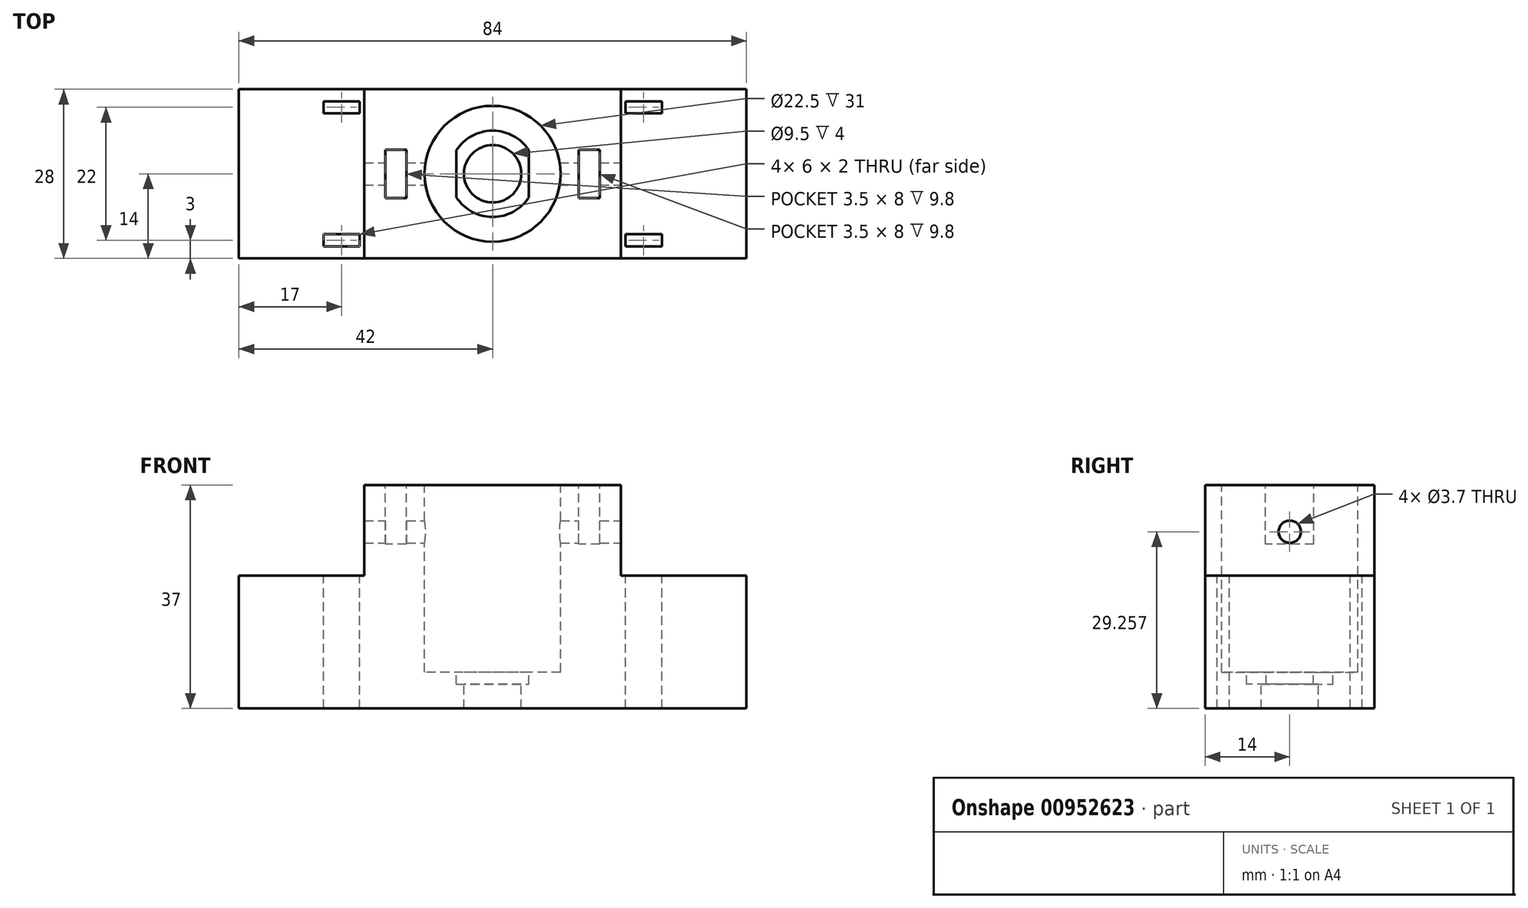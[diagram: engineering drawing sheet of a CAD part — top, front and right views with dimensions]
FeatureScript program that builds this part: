
annotation { "Feature Type Name" : "Feature", "Feature Type Description" : "" }
export const myFeature = defineFeature(function(context is Context, id is Id, definition is map)
    precondition{}
    {
        {
            var Q0;
            Q0=qCreatedBy(makeId("Top.planeOp"),FACE);
            var sketch = newSketch(context, id + "F0", { "sketchPlane" : qUnion([Q0])});
            skCircle(sketch, "E0", {"center": v(0, 0) * mm, "radius": 14 * mm});
            skLineSegment(sketch, "E1.bottom", {"start": v(42, -14) * mm, "end": v(-42, -14) * mm});
            skLineSegment(sketch, "E1.top", {"start": v(42, 14) * mm, "end": v(-42, 14) * mm});
            skLineSegment(sketch, "E1.left", {"start": v(42, -14) * mm, "end": v(42, 14) * mm});
            skLineSegment(sketch, "E1.right", {"start": v(-42, -14) * mm, "end": v(-42, 14) * mm});
            skSolve(sketch);
        }
        {
            var Q0;
            Q0 = qSketchRegion(id + "F0", true);
            var Q1;
            Q1 = qSketchRegion(id + "F3", true);
            var Q2;
            Q2 = qSketchRegion(id + "F2", true);
            extrude(context, id + "F1", {"entities" : qUnion([Q0, Q1, Q2]), "depth" : 22 * mm, "offsetDistance" : 25.4 * mm});
        }
        {
            var Q0;
            Q0=makeQuery(id+"F1.opExtrude","CAP_FACE",FACE,{"disambiguationData":[OSD([sQuery(id+"F0.wireOp",EDGE,"E1.bottom"),sQuery(id+"F0.wireOp",EDGE,"E1.top"),sQuery(id+"F0.wireOp",EDGE,"E1.left"),sQuery(id+"F0.wireOp",EDGE,"E1.right")])],"isStart":false});
            var sketch = newSketch(context, id + "F2", { "sketchPlane" : qUnion([Q0])});
            skArc(sketch, "E2", {"start": v(-6, -3.89) * mm, "mid": v(0, -7.15) * mm, "end": v(6, -3.89) * mm});
            skLineSegment(sketch, "E3.left", {"start": v(6, 3.89) * mm, "end": v(6, -3.89) * mm});
            skLineSegment(sketch, "E3.right", {"start": v(-6, 3.89) * mm, "end": v(-6, -3.89) * mm});
            skArc(sketch, "E4.trimOffspring", {"start": v(6, 3.89) * mm, "mid": v(0, 7.15) * mm, "end": v(-6, 3.89) * mm});
            skSolve(sketch);
        }
        {
            var Q0;
            Q0=makeQuery(id+"F1.opExtrude","CAP_FACE",FACE,{"disambiguationData":[OSD([sQuery(id+"F0.wireOp",EDGE,"E1.bottom"),sQuery(id+"F0.wireOp",EDGE,"E1.top"),sQuery(id+"F0.wireOp",EDGE,"E1.left"),sQuery(id+"F0.wireOp",EDGE,"E1.right")])],"isStart":false});
            var sketch = newSketch(context, id + "F3", { "sketchPlane" : qUnion([Q0])});
            skCircle(sketch, "E5", {"center": v(0, 0) * mm, "radius": 11.25 * mm});
            skSolve(sketch);
        }
        {
            var Q0;
            Q0 = qSketchRegion(id + "F3", true);
            extrude(context, id + "F4", {"entities" : qUnion([Q0]), "operationType" : NewBodyOperationType.REMOVE, "oppositeDirection" : true, "depth" : 16 * mm, "offsetDistance" : 25.4 * mm});
        }
        {
            var Q0;
            Q0 = qSketchRegion(id + "F2", true);
            extrude(context, id + "F5", {"entities" : qUnion([Q0]), "operationType" : NewBodyOperationType.REMOVE, "oppositeDirection" : true, "depth" : 18 * mm, "offsetDistance" : 25.4 * mm});
        }
        {
            var Q0;
            Q0=makeQuery(id+"F5.boolean.opBoolean","COPY",FACE,{"derivedFrom":makeQuery(id+"F5.opExtrude","CAP_FACE",FACE,{"disambiguationData":[OSD([sQuery(id+"F2.wireOp",EDGE,"E2"),sQuery(id+"F2.wireOp",EDGE,"E3.left"),sQuery(id+"F2.wireOp",EDGE,"E3.right"),sQuery(id+"F2.wireOp",EDGE,"E4.trimOffspring")])],"isStart":false})});
            var sketch = newSketch(context, id + "F6", { "sketchPlane" : qUnion([Q0])});
            skCircle(sketch, "E6", {"center": v(0, 0) * mm, "radius": 4.75 * mm});
            skSolve(sketch);
        }
        {
            var Q0;
            Q0 = qSketchRegion(id + "F6", true);
            extrude(context, id + "F7", {"entities" : qUnion([Q0]), "operationType" : NewBodyOperationType.REMOVE, "oppositeDirection" : true, "depth" : 4 * mm, "offsetDistance" : 25.4 * mm});
        }
        {
            var Q0;
            Q0=makeQuery(id+"F1.opExtrude","CAP_FACE",FACE,{"disambiguationData":[OSD([sQuery(id+"F0.wireOp",EDGE,"E1.bottom"),sQuery(id+"F0.wireOp",EDGE,"E1.top"),sQuery(id+"F0.wireOp",EDGE,"E1.left"),sQuery(id+"F0.wireOp",EDGE,"E1.right")])],"isStart":false});
            var sketch = newSketch(context, id + "F8", { "sketchPlane" : qUnion([Q0])});
            skPoint(sketch, "E7", {"position": v(-25, 0) * mm});
            skPoint(sketch, "E8", {"position": v(25, 0) * mm});
            skLineSegment(sketch, "E9", {"start": v(0, 0) * mm, "end": v(-25, 0) * mm});
            skLineSegment(sketch, "E10", {"start": v(-25, 0) * mm, "end": v(-25, 19.23) * mm});
            skLineSegment(sketch, "E11", {"start": v(-25, 0) * mm, "end": v(-25, -16.03) * mm});
            skLineSegment(sketch, "E12", {"start": v(25, 0) * mm, "end": v(25, 19.12) * mm});
            skLineSegment(sketch, "E13", {"start": v(25, 0) * mm, "end": v(25, -19.57) * mm});
            skPoint(sketch, "E14.orphan", {"position": v(-23.51, -11) * mm});
            skPoint(sketch, "E15", {"position": v(25, -11) * mm});
            skPoint(sketch, "E16", {"position": v(25, 11) * mm});
            skPoint(sketch, "E17", {"position": v(-25, 11) * mm});
            skPoint(sketch, "E18.orphan", {"position": v(23.65, -11) * mm});
            skLineSegment(sketch, "E19.bottom", {"start": v(28, -12) * mm, "end": v(22, -12) * mm});
            skLineSegment(sketch, "E19.top", {"start": v(28, -10) * mm, "end": v(22, -10) * mm});
            skLineSegment(sketch, "E19.left", {"start": v(28, -12) * mm, "end": v(28, -10) * mm});
            skLineSegment(sketch, "E19.right", {"start": v(22, -12) * mm, "end": v(22, -10) * mm});
            skPoint(sketch, "E20.start.orphan", {"position": v(23.65, 11) * mm});
            skLineSegment(sketch, "E21.bottom", {"start": v(28, 10) * mm, "end": v(22, 10) * mm});
            skLineSegment(sketch, "E21.top", {"start": v(28, 12) * mm, "end": v(22, 12) * mm});
            skLineSegment(sketch, "E21.left", {"start": v(28, 10) * mm, "end": v(28, 12) * mm});
            skLineSegment(sketch, "E21.right", {"start": v(22, 10) * mm, "end": v(22, 12) * mm});
            skPoint(sketch, "E22.start.orphan", {"position": v(-23.51, 11) * mm});
            skLineSegment(sketch, "E23.bottom", {"start": v(-22, 10) * mm, "end": v(-28, 10) * mm});
            skLineSegment(sketch, "E23.top", {"start": v(-22, 12) * mm, "end": v(-28, 12) * mm});
            skLineSegment(sketch, "E23.left", {"start": v(-22, 10) * mm, "end": v(-22, 12) * mm});
            skLineSegment(sketch, "E23.right", {"start": v(-28, 10) * mm, "end": v(-28, 12) * mm});
            skLineSegment(sketch, "E24.bottom", {"start": v(-22, -12) * mm, "end": v(-28, -12) * mm});
            skLineSegment(sketch, "E24.top", {"start": v(-22, -10) * mm, "end": v(-28, -10) * mm});
            skLineSegment(sketch, "E24.left", {"start": v(-22, -12) * mm, "end": v(-22, -10) * mm});
            skLineSegment(sketch, "E24.right", {"start": v(-28, -12) * mm, "end": v(-28, -10) * mm});
            skPoint(sketch, "E24.middle", {"position": v(-25, -11) * mm});
            skSolve(sketch);
        }
        {
            var Q0;
            Q0 = qSketchRegion(id + "F8", true);
            extrude(context, id + "F9", {"entities" : qUnion([Q0]), "operationType" : NewBodyOperationType.REMOVE, "oppositeDirection" : true, "depth" : 22 * mm, "offsetDistance" : 25.4 * mm});
        }
        {
            var Q0;
            Q0=makeQuery(id+"F1.opExtrude","CAP_FACE",FACE,{"disambiguationData":[OSD([sQuery(id+"F0.wireOp",EDGE,"E1.bottom"),sQuery(id+"F0.wireOp",EDGE,"E1.top"),sQuery(id+"F0.wireOp",EDGE,"E1.left"),sQuery(id+"F0.wireOp",EDGE,"E1.right")])],"isStart":false});
            var sketch = newSketch(context, id + "F10", { "sketchPlane" : qUnion([Q0])});
            skLineSegment(sketch, "E25.bottom", {"start": v(21.25, -14) * mm, "end": v(-21.25, -14) * mm});
            skLineSegment(sketch, "E25.top", {"start": v(21.25, 14) * mm, "end": v(-21.25, 14) * mm});
            skLineSegment(sketch, "E25.left", {"start": v(21.25, -14) * mm, "end": v(21.25, 14) * mm});
            skLineSegment(sketch, "E25.right", {"start": v(-21.25, -14) * mm, "end": v(-21.25, 14) * mm});
            skPoint(sketch, "E25.middle", {"position": v(0, 0) * mm});
            skLineSegment(sketch, "E26", {"start": v(11.25, 0) * mm, "end": v(21.25, 0) * mm});
            skSolve(sketch);
        }
        {
            var Q0;
            Q0 = qSketchRegion(id + "F10", true);
            extrude(context, id + "F11", {"entities" : qUnion([Q0]), "operationType" : NewBodyOperationType.ADD, "depth" : 15 * mm, "offsetDistance" : 25.4 * mm});
        }
        {
            var Q0;
            Q0=makeQuery(id+"F11.opExtrude","CAP_FACE",FACE,{"disambiguationData":[OSD([sQuery(id+"F10.wireOp",EDGE,"E25.bottom"),sQuery(id+"F10.wireOp",EDGE,"E25.top"),sQuery(id+"F10.wireOp",EDGE,"E25.left"),sQuery(id+"F10.wireOp",EDGE,"E25.right")])],"isStart":false});
            var sketch = newSketch(context, id + "F12", { "sketchPlane" : qUnion([Q0])});
            skCircle(sketch, "E27", {"center": v(0, 0) * mm, "radius": 11.25 * mm});
            skSolve(sketch);
        }
        {
            var Q0;
            Q0 = qSketchRegion(id + "F12", true);
            extrude(context, id + "F13", {"entities" : qUnion([Q0]), "operationType" : NewBodyOperationType.REMOVE, "oppositeDirection" : true, "depth" : 15 * mm, "offsetDistance" : 25.4 * mm});
        }
        {
            var Q0;
            Q0=makeQuery(id+"F11.opExtrude","SWEPT_FACE",FACE,{"disambiguationData":[OSD([sQuery(id+"F10.wireOp",EDGE,"E25.left")])]});
            var sketch = newSketch(context, id + "F14", { "sketchPlane" : qUnion([Q0])});
            skCircle(sketch, "E28", {"center": v(0, 29.26) * mm, "radius": 1.85 * mm});
            skSolve(sketch);
        }
        {
            var Q0;
            Q0 = qSketchRegion(id + "F14", true);
            extrude(context, id + "F15", {"entities" : qUnion([Q0]), "operationType" : NewBodyOperationType.REMOVE, "oppositeDirection" : true, "depth" : 50.8 * mm, "offsetDistance" : 25.4 * mm});
        }
        {
            var Q0;
            Q0=makeQuery(id+"F11.opExtrude","CAP_FACE",FACE,{"disambiguationData":[OSD([sQuery(id+"F10.wireOp",EDGE,"E25.bottom"),sQuery(id+"F10.wireOp",EDGE,"E25.top"),sQuery(id+"F10.wireOp",EDGE,"E25.left"),sQuery(id+"F10.wireOp",EDGE,"E25.right")])],"isStart":false});
            var sketch = newSketch(context, id + "F16", { "sketchPlane" : qUnion([Q0])});
            skLineSegment(sketch, "E29.bottom", {"start": v(-14.25, 4) * mm, "end": v(-17.75, 4) * mm});
            skLineSegment(sketch, "E29.top", {"start": v(-14.25, -4) * mm, "end": v(-17.75, -4) * mm});
            skLineSegment(sketch, "E29.left", {"start": v(-14.25, 4) * mm, "end": v(-14.25, -4) * mm});
            skLineSegment(sketch, "E29.right", {"start": v(-17.75, 4) * mm, "end": v(-17.75, -4) * mm});
            skPoint(sketch, "E29.middle", {"position": v(-16, 0) * mm});
            skLineSegment(sketch, "E30", {"start": v(-17.75, 1.2) * mm, "end": v(-21.25, 1.2) * mm});
            skLineSegment(sketch, "E31.bottom", {"start": v(17.75, -4) * mm, "end": v(14.25, -4) * mm});
            skLineSegment(sketch, "E31.top", {"start": v(17.75, 4) * mm, "end": v(14.25, 4) * mm});
            skLineSegment(sketch, "E31.left", {"start": v(17.75, -4) * mm, "end": v(17.75, 4) * mm});
            skLineSegment(sketch, "E31.right", {"start": v(14.25, -4) * mm, "end": v(14.25, 4) * mm});
            skPoint(sketch, "E31.middle", {"position": v(16, 0) * mm});
            skLineSegment(sketch, "E32", {"start": v(17.75, 0) * mm, "end": v(21.25, 0) * mm});
            skSolve(sketch);
        }
        {
            var Q0;
            Q0 = qSketchRegion(id + "F16", true);
            extrude(context, id + "F17", {"entities" : qUnion([Q0]), "operationType" : NewBodyOperationType.REMOVE, "oppositeDirection" : true, "depth" : 9.8 * mm, "offsetDistance" : 25.4 * mm});
        }
    });
